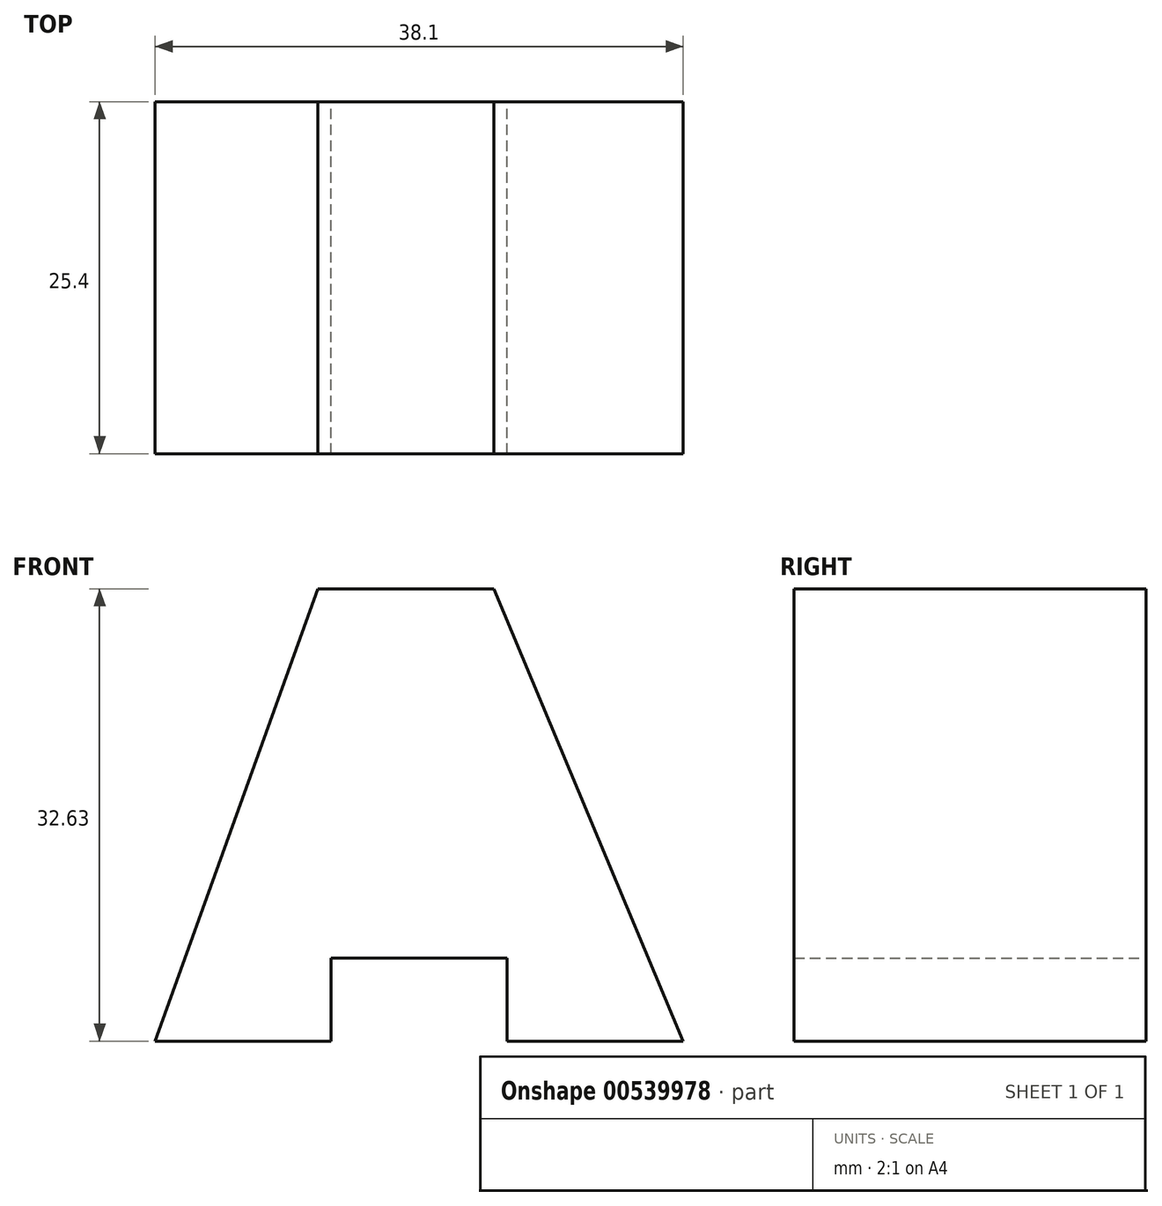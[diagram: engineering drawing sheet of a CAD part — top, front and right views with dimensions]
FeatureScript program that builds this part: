
annotation { "Feature Type Name" : "Feature", "Feature Type Description" : "" }
export const myFeature = defineFeature(function(context is Context, id is Id, definition is map)
    precondition{}
    {
        {
            var Q0;
            Q0=qCreatedBy(makeId("Front.planeOp"),FACE);
            var sketch = newSketch(context, id + "F0", { "sketchPlane" : qUnion([Q0])});
            skLineSegment(sketch, "E0", {"start": v(-44.45, 0) * mm, "end": v(-31.75, 0) * mm});
            skLineSegment(sketch, "E1", {"start": v(-31.75, 0) * mm, "end": v(-31.75, 5.98) * mm});
            skLineSegment(sketch, "E2", {"start": v(-31.75, 5.98) * mm, "end": v(-19.05, 5.98) * mm});
            skLineSegment(sketch, "E3", {"start": v(-19.05, 5.98) * mm, "end": v(-19.05, 0) * mm});
            skLineSegment(sketch, "E4", {"start": v(-19.05, 0) * mm, "end": v(-6.35, 0) * mm});
            skLineSegment(sketch, "E5", {"start": v(-32.7, 32.63) * mm, "end": v(-20, 32.63) * mm});
            skLineSegment(sketch, "E6", {"start": v(-20, 32.63) * mm, "end": v(-6.35, 0) * mm});
            skLineSegment(sketch, "E7", {"start": v(-32.7, 32.63) * mm, "end": v(-44.45, 0) * mm});
            skSolve(sketch);
        }
        {
            var Q0;
            Q0=makeQuery(id+"F0.imprint","IMPRINT",FACE,{"disambiguationData":[TD([[makeQuery(id+"F0.imprint","IMPRINT",EDGE,{"derivedFrom":sQuery(id+"F0.wireOp",EDGE,"E0")}),1.0]])]});
            extrude(context, id + "F1", {"entities" : qUnion([Q0]), "depth" : 25.4 * mm, "offsetDistance" : 25.4 * mm});
        }
    });
